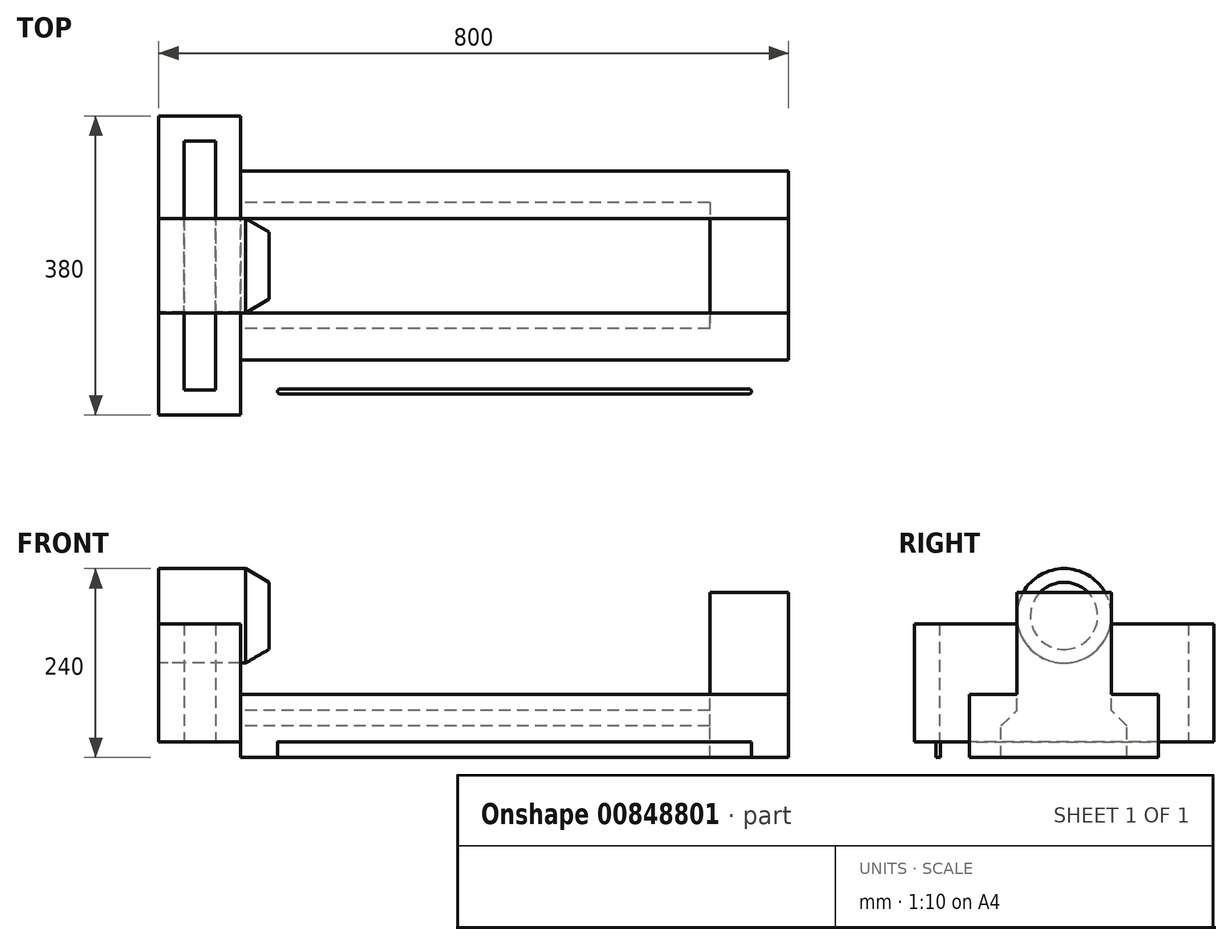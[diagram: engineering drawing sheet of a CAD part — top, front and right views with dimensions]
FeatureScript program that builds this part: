
annotation { "Feature Type Name" : "Feature", "Feature Type Description" : "" }
export const myFeature = defineFeature(function(context is Context, id is Id, definition is map)
    precondition{}
    {
        {
            var Q0;
            Q0=qCreatedBy(makeId("Top.planeOp"),FACE);
            var sketch = newSketch(context, id + "F0", { "sketchPlane" : qUnion([Q0])});
            skLineSegment(sketch, "E0.bottom", {"start": v(400, 200) * mm, "end": v(-400, 200) * mm});
            skLineSegment(sketch, "E0.top", {"start": v(400, -200) * mm, "end": v(-400, -200) * mm});
            skLineSegment(sketch, "E0.left", {"start": v(400, 200) * mm, "end": v(400, -200) * mm});
            skLineSegment(sketch, "E0.right", {"start": v(-400, 200) * mm, "end": v(-400, -200) * mm});
            skPoint(sketch, "E0.middle", {"position": v(0, 0) * mm});
            skSolve(sketch);
        }
        {
            var Q0;
            Q0=qSketchRegion(id+"F0",true);
            extrude(context, id + "F1", {"entities" : qUnion([Q0]), "depth" : 20 * mm, "offsetDistance" : 25 * mm});
        }
        {
            var Q0;
            Q0=makeQuery(id+"F1.opExtrude","CAP_FACE",FACE,{"disambiguationData":[OSD([sQuery(id+"F0.wireOp",EDGE,"E0.bottom"),sQuery(id+"F0.wireOp",EDGE,"E0.top"),sQuery(id+"F0.wireOp",EDGE,"E0.left"),sQuery(id+"F0.wireOp",EDGE,"E0.right")])],"isStart":false});
            var sketch = newSketch(context, id + "F2", { "sketchPlane" : qUnion([Q0])});
            skLineSegment(sketch, "E1.bottom", {"start": v(-400, -190) * mm, "end": v(-368, -190) * mm});
            skLineSegment(sketch, "E1.top", {"start": v(-400, 190) * mm, "end": v(-368, 190) * mm});
            skLineSegment(sketch, "E1.left", {"start": v(-400, -190) * mm, "end": v(-400, 190) * mm});
            skLineSegment(sketch, "E1.right", {"start": v(-368, -190) * mm, "end": v(-368, 190) * mm});
            skLineSegment(sketch, "E2.bottom", {"start": v(-328, 190) * mm, "end": v(-296, 190) * mm});
            skLineSegment(sketch, "E2.top", {"start": v(-328, -190) * mm, "end": v(-296, -190) * mm});
            skLineSegment(sketch, "E2.left", {"start": v(-328, 190) * mm, "end": v(-328, -190) * mm});
            skLineSegment(sketch, "E2.right", {"start": v(-296, 190) * mm, "end": v(-296, -190) * mm});
            skLineSegment(sketch, "E3.bottom", {"start": v(-368, 190) * mm, "end": v(-328, 190) * mm});
            skLineSegment(sketch, "E3.top", {"start": v(-368, 158) * mm, "end": v(-328, 158) * mm});
            skLineSegment(sketch, "E3.left", {"start": v(-368, 190) * mm, "end": v(-368, 158) * mm});
            skLineSegment(sketch, "E3.right", {"start": v(-328, 190) * mm, "end": v(-328, 158) * mm});
            skLineSegment(sketch, "E4.bottom", {"start": v(-368, -190) * mm, "end": v(-328, -190) * mm});
            skLineSegment(sketch, "E4.top", {"start": v(-368, -158) * mm, "end": v(-328, -158) * mm});
            skLineSegment(sketch, "E4.left", {"start": v(-368, -190) * mm, "end": v(-368, -158) * mm});
            skLineSegment(sketch, "E4.right", {"start": v(-328, -190) * mm, "end": v(-328, -158) * mm});
            skSolve(sketch);
        }
        {
            var Q0;
            {var subQ0=sQuery(id+"F2.wireOp",EDGE,"E3.bottom");var subQ7=sQuery(id+"F2.wireOp",EDGE,"E2.bottom");var subQ10=sQuery(id+"F2.wireOp",EDGE,"E4.bottom");var subQ11=sQuery(id+"F2.wireOp",EDGE,"E1.bottom");Q0=qUnion([makeQuery(id+"F2.imprint","IMPRINT",FACE,{"disambiguationData":[TD([[makeQuery(id+"F2.imprint","IMPRINT",EDGE,{"derivedFrom":subQ11}),1.0]])]}),makeQuery(id+"F2.imprint","IMPRINT",FACE,{"disambiguationData":[TD([[makeQuery(id+"F2.imprint","IMPRINT",EDGE,{"derivedFrom":subQ7}),-1.0]])]}),makeQuery(id+"F2.imprint","IMPRINT",FACE,{"disambiguationData":[TD([[makeQuery(id+"F2.imprint","IMPRINT",EDGE,{"derivedFrom":subQ10}),1.0]])]}),makeQuery(id+"F2.imprint","IMPRINT",FACE,{"disambiguationData":[TD([[makeQuery(id+"F2.imprint","IMPRINT",EDGE,{"derivedFrom":subQ0}),-1.0]])]})]);}
            extrude(context, id + "F3", {"entities" : qUnion([Q0]), "depth" : 150 * mm, "offsetDistance" : 25 * mm});
        }
        {
            var Q0;
            Q0=makeQuery(id+"F3.opExtrude","SWEPT_FACE",FACE,{"disambiguationData":[OSD([sQuery(id+"F2.wireOp",EDGE,"E1.left")])]});
            var sketch = newSketch(context, id + "F4", { "sketchPlane" : qUnion([Q0])});
            skCircle(sketch, "E5", {"center": v(0, 180) * mm, "radius": 60 * mm});
            skSolve(sketch);
        }
        {
            var Q0;
            {var subQ0=sQuery(id+"F4.wireOp",EDGE,"E5");var subQ1=makeQuery(id+"F3.opExtrude","CAP_EDGE",EDGE,{"disambiguationData":[OSD([sQuery(id+"F2.wireOp",EDGE,"E1.left")])],"isStart":false});var subQ2=makeQuery(id+"F4.imprint","INTERSECT",VERTEX,{"disambiguationData":[OD(0.0)],"derivedFrom":[subQ1,subQ0]});Q0=makeQuery(id+"F4.imprint","IMPRINT",FACE,{"disambiguationData":[TD([[makeQuery(id+"F4.imprint","IMPRINT",EDGE,{"disambiguationData":[TD([[subQ2,-1.0]])],"derivedFrom":subQ0}),1.0]])]});}
            var Q1;
            {var subQ0=sQuery(id+"F4.wireOp",EDGE,"E5");var subQ1=makeQuery(id+"F3.opExtrude","CAP_EDGE",EDGE,{"disambiguationData":[OSD([sQuery(id+"F2.wireOp",EDGE,"E1.left")])],"isStart":false});var subQ2=makeQuery(id+"F4.imprint","INTERSECT",VERTEX,{"disambiguationData":[OD(0.0)],"derivedFrom":[subQ1,subQ0]});Q1=makeQuery(id+"F4.imprint","IMPRINT",FACE,{"disambiguationData":[TD([[makeQuery(id+"F4.imprint","IMPRINT",EDGE,{"disambiguationData":[TD([[subQ2,1.0]])],"derivedFrom":subQ0}),1.0]])]});}
            extrude(context, id + "F5", {"entities" : qUnion([Q0, Q1]), "operationType" : NewBodyOperationType.REMOVE, "endBound" : BoundingType.THROUGH_ALL, "oppositeDirection" : true, "depth" : 25 * mm, "offsetDistance" : 25 * mm});
        }
        {
            var Q0;
            Q0=makeQuery(id+"F3.opExtrude","SWEPT_FACE",FACE,{"disambiguationData":[OSD([sQuery(id+"F2.wireOp",EDGE,"E1.left")])]});
            var sketch = newSketch(context, id + "F6", { "sketchPlane" : qUnion([Q0])});
            skCircle(sketch, "E6", {"center": v(0, 180) * mm, "radius": 60 * mm});
            skSolve(sketch);
        }
        {
            var Q0;
            Q0 = qSketchRegion(id + "F6", true);
            extrude(context, id + "F7", {"entities" : qUnion([Q0]), "oppositeDirection" : true, "depth" : 110 * mm, "offsetDistance" : 25 * mm});
        }
        {
            var Q0;
            Q0=makeQuery(id+"F7.opExtrude","CAP_FACE",FACE,{"disambiguationData":[OSD([sQuery(id+"F6.wireOp",EDGE,"E6")])],"isStart":false});
            var sketch = newSketch(context, id + "F8", { "sketchPlane" : qUnion([Q0])});
            skCircle(sketch, "E7.0", {"center": v(0, 180) * mm, "radius": 60 * mm});
            skSolve(sketch);
        }
        {
            var Q0;
            Q0 = qSketchRegion(id + "F8", true);
            extrude(context, id + "F9", {"entities" : qUnion([Q0]), "operationType" : NewBodyOperationType.ADD, "depth" : 30 * mm, "offsetDistance" : 25 * mm, "hasDraft" : true, "draftAngle" : 30 * degree, "draftPullDirection" : true});
        }
        {
            var Q0;
            Q0=makeQuery(id+"F3.opExtrude","SWEPT_FACE",FACE,{"disambiguationData":[OSD([sQuery(id+"F2.wireOp",EDGE,"E2.right")])]});
            var sketch = newSketch(context, id + "F10", { "sketchPlane" : qUnion([Q0])});
            skLineSegment(sketch, "E8", {"start": v(-80, 20) * mm, "end": v(-80, 20) * mm});
            skLineSegment(sketch, "E9", {"start": v(-80, 20) * mm, "end": v(-80, 40) * mm});
            skLineSegment(sketch, "E10", {"start": v(-80, 40) * mm, "end": v(-60, 60) * mm});
            skLineSegment(sketch, "E11", {"start": v(-60, 60) * mm, "end": v(-60, 80) * mm});
            skLineSegment(sketch, "E12", {"start": v(-60, 80) * mm, "end": v(-120, 80) * mm});
            skLineSegment(sketch, "E13", {"start": v(-120, 80) * mm, "end": v(-120, 20) * mm});
            skLineSegment(sketch, "E14", {"start": v(-120, 20) * mm, "end": v(-80, 20) * mm});
            skSolve(sketch);
        }
        {
            var Q0;
            Q0 = qSketchRegion(id + "F10", true);
            var Q1;
            Q1=makeQuery(id+"F1.opExtrude","SWEPT_FACE",FACE,{"disambiguationData":[OSD([sQuery(id+"F0.wireOp",EDGE,"E0.left")])]});
            extrude(context, id + "F11", {"entities" : qUnion([Q0]), "endBound" : BoundingType.UP_TO_SURFACE, "depth" : 25 * mm, "endBoundEntityFace" : qUnion([Q1]), "offsetDistance" : 25 * mm});
        }
        {
            var Q0;
            Q0=makeQuery(id+"F11.opExtrude","SWEPT_BODY",BODY,{"disambiguationData":[OSD([sQuery(id+"F10.wireOp",EDGE,"E9"),sQuery(id+"F10.wireOp",EDGE,"E10"),sQuery(id+"F10.wireOp",EDGE,"E11"),sQuery(id+"F10.wireOp",EDGE,"E12"),sQuery(id+"F10.wireOp",EDGE,"E13"),sQuery(id+"F10.wireOp",EDGE,"E14")])]});
            var Q1;
            Q1=qCreatedBy(makeId("Front.planeOp"),FACE);
            mirror(context, id + "F12", {"entities" : qUnion([Q0]), "mirrorPlane" : qUnion([Q1])});
        }
        {
            var Q0;
            Q0=makeQuery(id+"F1.opExtrude","SWEPT_FACE",FACE,{"disambiguationData":[OSD([sQuery(id+"F0.wireOp",EDGE,"E0.left")])]});
            var sketch = newSketch(context, id + "F13", { "sketchPlane" : qUnion([Q0])});
            skLineSegment(sketch, "E15", {"start": v(-80, 20) * mm, "end": v(-80, 40) * mm});
            skLineSegment(sketch, "E16", {"start": v(-80, 40) * mm, "end": v(-60, 60) * mm});
            skLineSegment(sketch, "E17", {"start": v(-60, 60) * mm, "end": v(-60, 210) * mm});
            skLineSegment(sketch, "E18", {"start": v(-60, 210) * mm, "end": v(0, 210) * mm});
            skLineSegment(sketch, "E19", {"start": v(0, 210) * mm, "end": v(0, 20) * mm});
            skLineSegment(sketch, "E20", {"start": v(0, 20) * mm, "end": v(-80, 20) * mm});
            skSolve(sketch);
        }
        {
            var Q0;
            Q0 = qSketchRegion(id + "F13", true);
            extrude(context, id + "F14", {"entities" : qUnion([Q0]), "oppositeDirection" : true, "depth" : 100 * mm, "offsetDistance" : 25 * mm});
        }
        {
            var Q0;
            Q0=makeQuery(id+"F14.opExtrude","SWEPT_BODY",BODY,{"disambiguationData":[OSD([sQuery(id+"F13.wireOp",EDGE,"E15"),sQuery(id+"F13.wireOp",EDGE,"E16"),sQuery(id+"F13.wireOp",EDGE,"E17"),sQuery(id+"F13.wireOp",EDGE,"E18"),sQuery(id+"F13.wireOp",EDGE,"E19"),sQuery(id+"F13.wireOp",EDGE,"E20")])]});
            var Q1;
            Q1=makeQuery(id+"F14.opExtrude","SWEPT_FACE",FACE,{"disambiguationData":[OSD([sQuery(id+"F13.wireOp",EDGE,"E19")])]});
            mirror(context, id + "F15", {"operationType" : NewBodyOperationType.ADD, "entities" : qUnion([Q0]), "mirrorPlane" : qUnion([Q1])});
        }
        {
            var Q0;
            Q0=makeQuery(id+"F1.opExtrude","CAP_FACE",FACE,{"disambiguationData":[OSD([sQuery(id+"F0.wireOp",EDGE,"E0.bottom"),sQuery(id+"F0.wireOp",EDGE,"E0.top"),sQuery(id+"F0.wireOp",EDGE,"E0.left"),sQuery(id+"F0.wireOp",EDGE,"E0.right")])],"isStart":false});
            var sketch = newSketch(context, id + "F16", { "sketchPlane" : qUnion([Q0])});
            skLineSegment(sketch, "E21", {"start": v(-246, -160) * mm, "end": v(350, -160) * mm});
            skArc(sketch, "E22.0.startCap", {"start": v(-246, -163) * mm, "mid": v(-249, -160) * mm, "end": v(-246, -157) * mm});
            skArc(sketch, "E22.0.endCap", {"start": v(350, -157) * mm, "mid": v(353, -160) * mm, "end": v(350, -163) * mm});
            skLineSegment(sketch, "E22.0.left", {"start": v(-246, -157) * mm, "end": v(350, -157) * mm});
            skLineSegment(sketch, "E22.0.right", {"start": v(-246, -163) * mm, "end": v(350, -163) * mm});
            skSolve(sketch);
        }
        {
            var Q0;
            Q0=makeQuery(id+"F16.imprint","IMPRINT",FACE,{"disambiguationData":[TD([[makeQuery(id+"F16.imprint","IMPRINT",EDGE,{"derivedFrom":sQuery(id+"F16.wireOp",EDGE,"E22.0.startCap")}),-1.0]])]});
            extrude(context, id + "F17", {"entities" : qUnion([Q0]), "operationType" : NewBodyOperationType.REMOVE, "endBound" : BoundingType.THROUGH_ALL, "oppositeDirection" : true, "depth" : 25 * mm, "offsetDistance" : 25 * mm});
        }
    });
